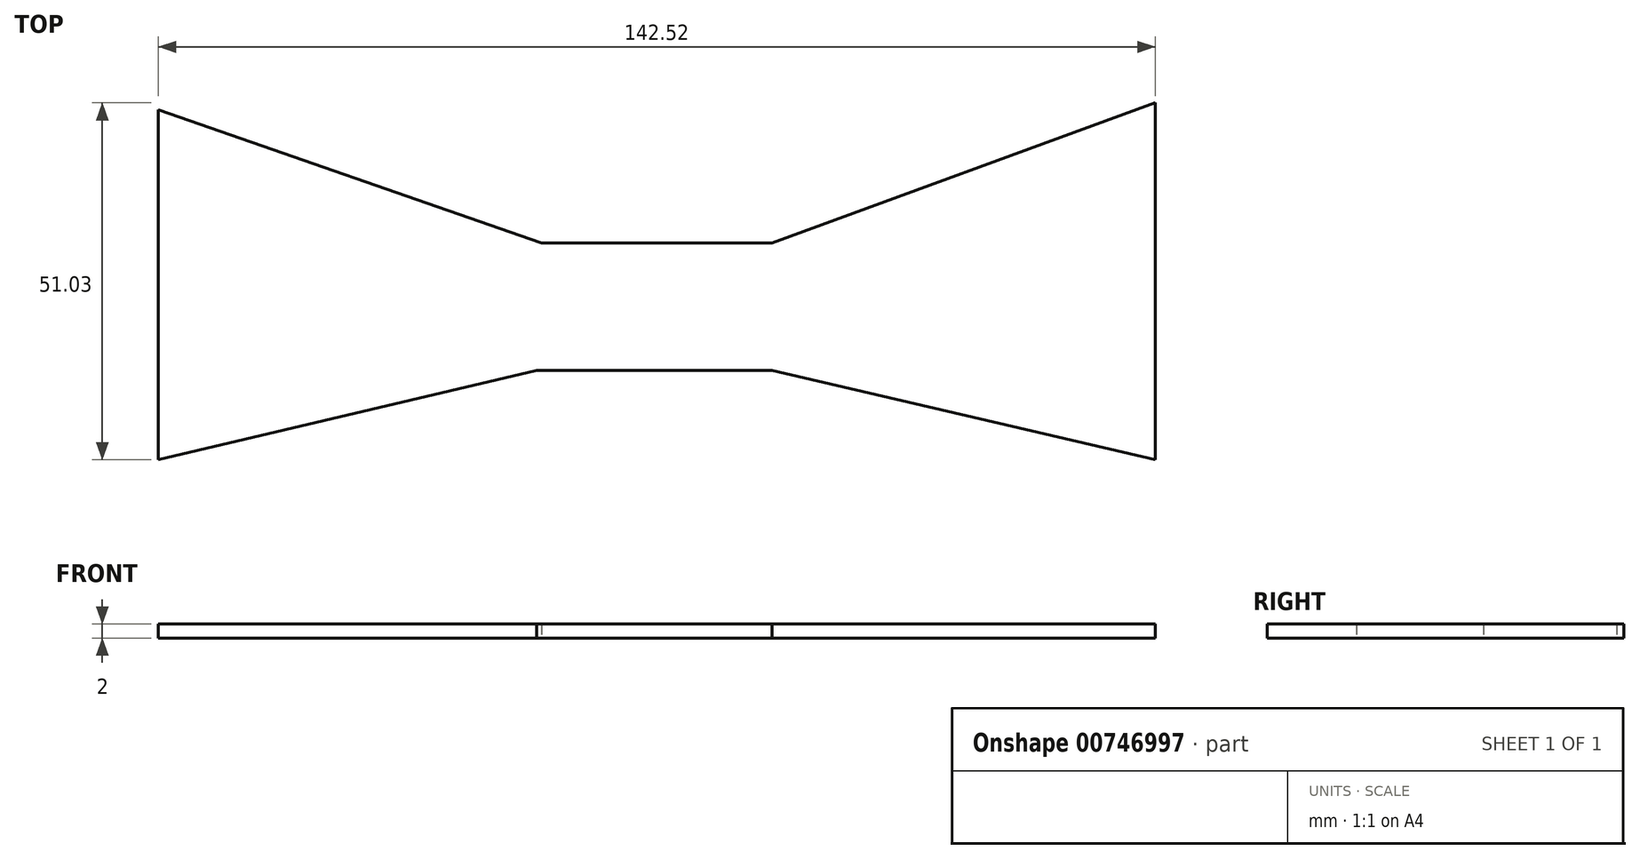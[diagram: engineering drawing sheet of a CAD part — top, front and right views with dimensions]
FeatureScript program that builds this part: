
annotation { "Feature Type Name" : "Feature", "Feature Type Description" : "" }
export const myFeature = defineFeature(function(context is Context, id is Id, definition is map)
    precondition{}
    {
        {
            var Q0;
            Q0=qCreatedBy(makeId("Top.planeOp"),FACE);
            var sketch = newSketch(context, id + "F0", { "sketchPlane" : qUnion([Q0])});
            skLineSegment(sketch, "E0", {"start": v(-73.3, 37.24) * mm, "end": v(-73.3, -12.76) * mm});
            skLineSegment(sketch, "E1", {"start": v(-73.3, -12.76) * mm, "end": v(-19.22, 0) * mm});
            skLineSegment(sketch, "E2", {"start": v(-19.22, 0) * mm, "end": v(14.46, 0) * mm});
            skLineSegment(sketch, "E3", {"start": v(14.46, 0) * mm, "end": v(69.22, -12.76) * mm});
            skLineSegment(sketch, "E4", {"start": v(69.22, -12.76) * mm, "end": v(69.22, 38.27) * mm});
            skLineSegment(sketch, "E5", {"start": v(69.22, 38.27) * mm, "end": v(14.46, 18.2) * mm});
            skLineSegment(sketch, "E6", {"start": v(14.46, 18.2) * mm, "end": v(-18.54, 18.2) * mm});
            skLineSegment(sketch, "E7", {"start": v(-18.54, 18.2) * mm, "end": v(-73.3, 37.24) * mm});
            skSolve(sketch);
        }
        {
            var Q0;
            Q0=makeQuery(id+"F0.imprint","IMPRINT",FACE,{"disambiguationData":[TD([[makeQuery(id+"F0.imprint","IMPRINT",EDGE,{"derivedFrom":sQuery(id+"F0.wireOp",EDGE,"E0")}),1.0]])]});
            extrude(context, id + "F1", {"entities" : qUnion([Q0]), "depth" : 2 * mm, "offsetDistance" : 25 * mm});
        }
    });
